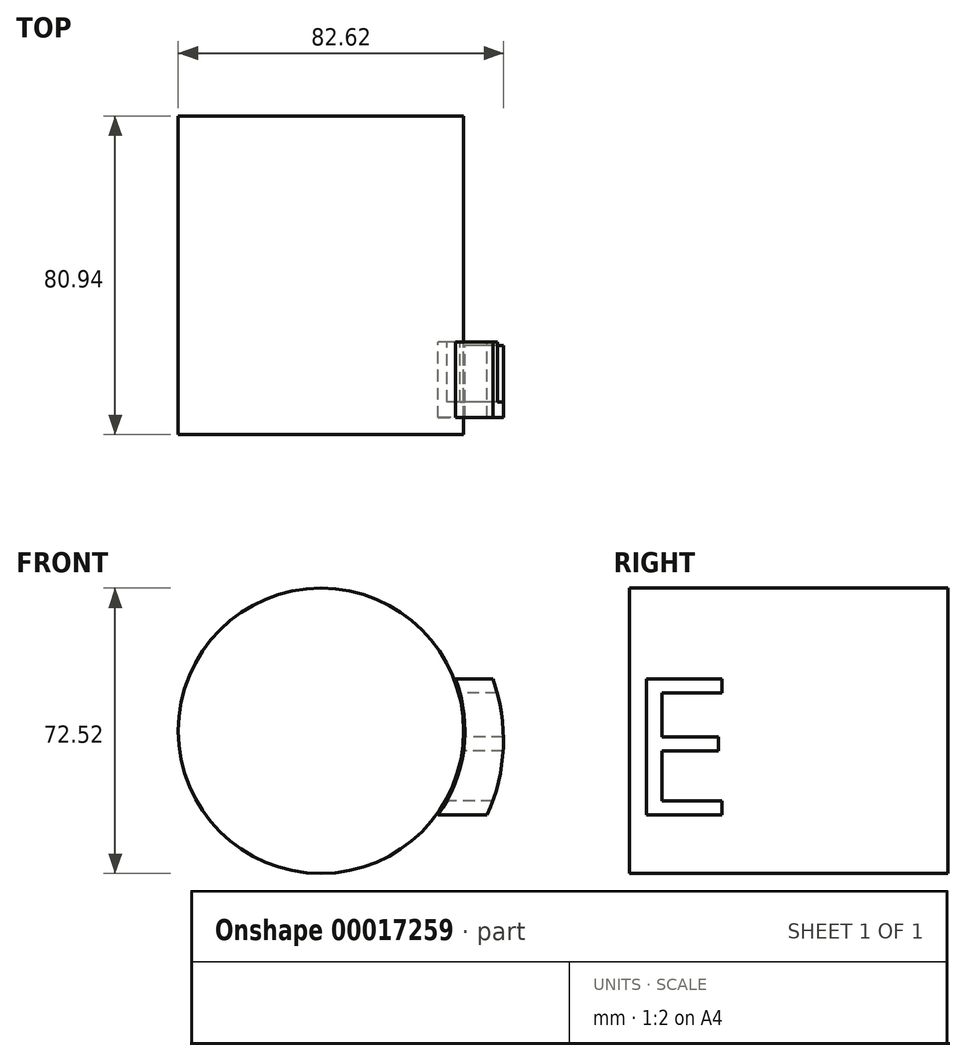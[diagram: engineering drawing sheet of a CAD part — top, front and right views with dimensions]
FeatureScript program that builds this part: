
annotation { "Feature Type Name" : "Feature", "Feature Type Description" : "" }
export const myFeature = defineFeature(function(context is Context, id is Id, definition is map)
    precondition{}
    {
        {
            var Q0;
            Q0=qCreatedBy(makeId("Front.planeOp"),FACE);
            var sketch = newSketch(context, id + "F0", { "sketchPlane" : qUnion([Q0])});
            skCircle(sketch, "E0", {"center": v(0, -2.28) * mm, "radius": 46.36 * mm});
            skCircle(sketch, "E1", {"center": v(0, 0) * mm, "radius": 36.59 * mm});
            skSolve(sketch);
        }
        {
            var Q0;
            Q0=makeQuery(id+"F0.imprint","IMPRINT",FACE,{"disambiguationData":[TD([[makeQuery(id+"F0.imprint","IMPRINT",EDGE,{"derivedFrom":sQuery(id+"F0.wireOp",EDGE,"E0")}),1.0]])]});
            extrude(context, id + "F1", {"entities" : qUnion([Q0]), "depth" : 83.46 * mm});
        }
        {
            var Q0;
            Q0=qCreatedBy(makeId("Right.planeOp"),FACE);
            var sketch = newSketch(context, id + "F2", { "sketchPlane" : qUnion([Q0])});
            skText(sketch, "E2", { "text": "E", "fontName": "OpenSans-Regular.ttf"});
            const initialGuessF2  = {"E2": [-0.056, -0.0214, 1, 0, 0.03485]};
            skSetInitialGuess(sketch, initialGuessF2);
            skSolve(sketch);
        }
        {
            var Q0;
            Q0 = qSketchRegion(id + "F2", true);
            extrude(context, id + "F3", {"entities" : qUnion([Q0]), "operationType" : NewBodyOperationType.INTERSECT, "depth" : 51.45 * mm});
        }
        {
            var Q0;
            Q0=qCreatedBy(makeId("Front.planeOp"),FACE);
            var sketch = newSketch(context, id + "F4", { "sketchPlane" : qUnion([Q0])});
            skCircle(sketch, "E3", {"center": v(0, 0) * mm, "radius": 36.26 * mm});
            skSolve(sketch);
        }
        {
            var Q0;
            Q0=makeQuery(id+"F4.imprint","IMPRINT",FACE,{"disambiguationData":[TD([[makeQuery(id+"F4.imprint","IMPRINT",EDGE,{"derivedFrom":sQuery(id+"F4.wireOp",EDGE,"E3")}),1.0]])]});
            extrude(context, id + "F5", {"entities" : qUnion([Q0]), "depth" : 55.54 * mm, "hasSecondDirection" : true, "secondDirectionOppositeDirection" : true, "secondDirectionDepth" : 25.4 * mm});
        }
    });
